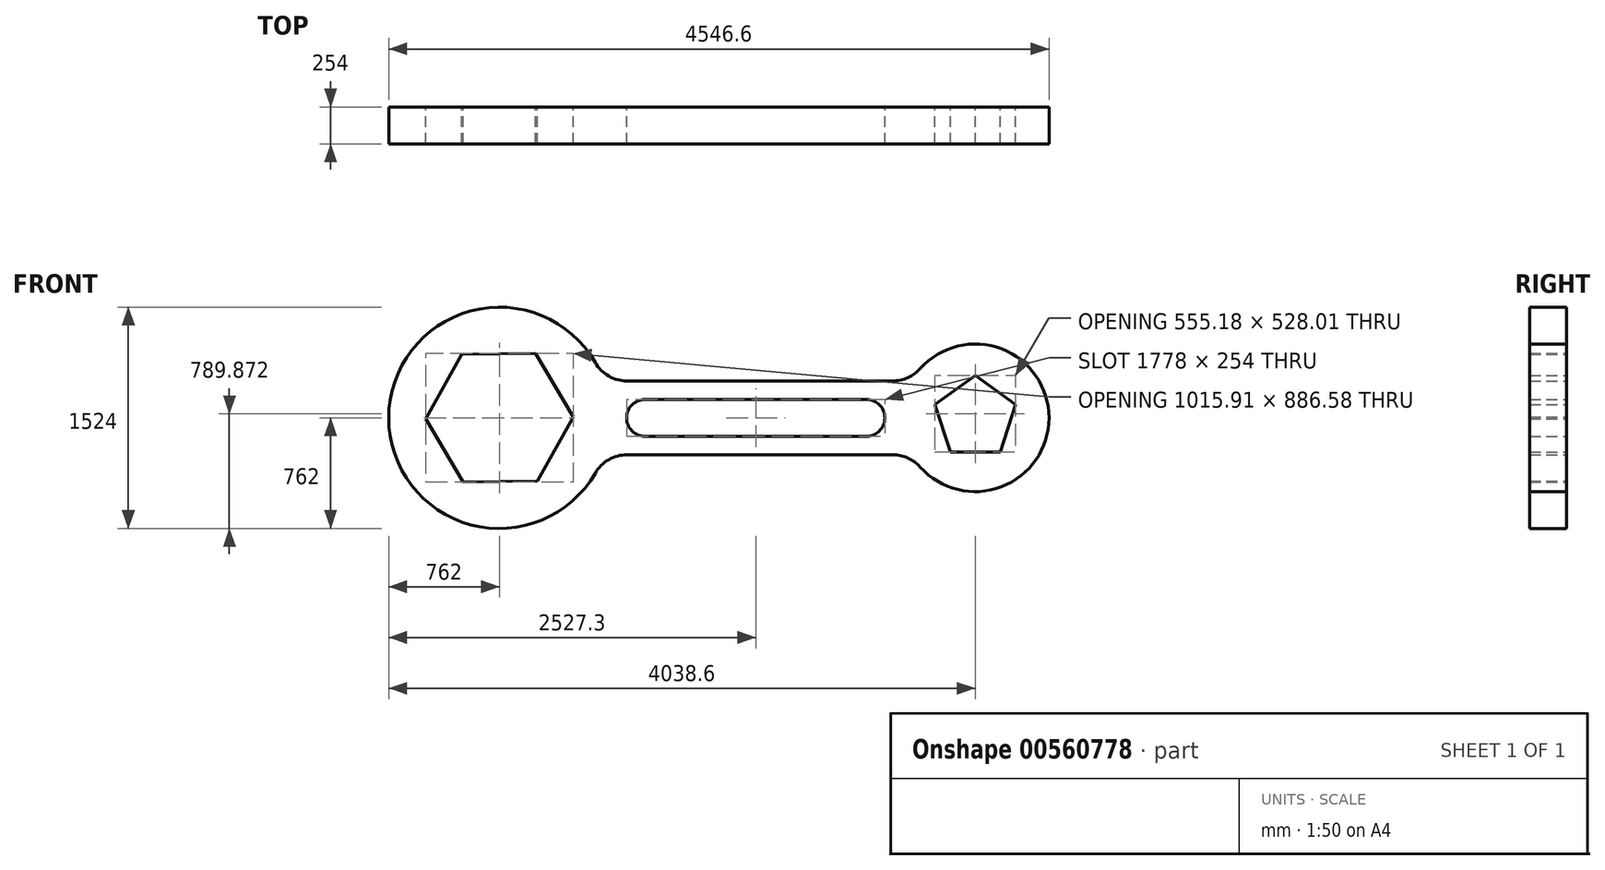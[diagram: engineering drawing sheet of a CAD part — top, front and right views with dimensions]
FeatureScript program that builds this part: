
annotation { "Feature Type Name" : "Feature", "Feature Type Description" : "" }
export const myFeature = defineFeature(function(context is Context, id is Id, definition is map)
    precondition{}
    {
        {
            var Q0;
            Q0=qCreatedBy(makeId("Front.planeOp"),FACE);
            var sketch = newSketch(context, id + "F0", { "sketchPlane" : qUnion([Q0])});
            skCircle(sketch, "E0", {"center": v(0, 0) * mm, "radius": 762 * mm});
            skCircle(sketch, "E1", {"center": v(3276.6, 0) * mm, "radius": 508 * mm});
            skLineSegment(sketch, "E2", {"start": v(1765.3, -254) * mm, "end": v(2708.64, -254) * mm});
            skLineSegment(sketch, "E3", {"start": v(1765.3, -254) * mm, "end": v(879.88, -254) * mm});
            skLineSegment(sketch, "E4", {"start": v(1765.3, 254) * mm, "end": v(879.88, 254) * mm});
            skLineSegment(sketch, "E5", {"start": v(1765.3, 254) * mm, "end": v(2708.64, 254) * mm});
            skArc(sketch, "E6", {"start": v(879.88, -254) * mm, "mid": v(752.88, -288.03) * mm, "end": v(659.91, -381) * mm});
            skArc(sketch, "E7", {"start": v(659.91, 381) * mm, "mid": v(752.88, 288.03) * mm, "end": v(879.88, 254) * mm});
            skArc(sketch, "E8", {"start": v(2708.64, 254) * mm, "mid": v(2812.33, 276.13) * mm, "end": v(2897.96, 338.67) * mm});
            skArc(sketch, "E9", {"start": v(2897.96, -338.67) * mm, "mid": v(2812.33, -276.13) * mm, "end": v(2708.64, -254) * mm});
            skPoint(sketch, "E10.orphan", {"position": v(762, 0) * mm});
            skPoint(sketch, "E11.orphan", {"position": v(2768.6, 0) * mm});
            skPoint(sketch, "E12.orphan", {"position": v(2654.3, 127) * mm});
            skLineSegment(sketch, "E13", {"start": v(1765.3, 127) * mm, "end": v(1003.3, 127) * mm});
            skLineSegment(sketch, "E14", {"start": v(1003.3, -127) * mm, "end": v(2527.3, -127) * mm});
            skLineSegment(sketch, "E15", {"start": v(2527.3, 127) * mm, "end": v(1765.3, 127) * mm});
            skArc(sketch, "E16", {"start": v(1003.3, 127) * mm, "mid": v(876.3, 0) * mm, "end": v(1003.3, -127) * mm});
            skArc(sketch, "E17", {"start": v(2527.3, -127) * mm, "mid": v(2654.3, 0) * mm, "end": v(2527.3, 127) * mm});
            skPoint(sketch, "E18.start.orphan", {"position": v(1765.3, 0) * mm});
            skLineSegment(sketch, "E19.0", {"start": v(248.1, 443.3) * mm, "end": v(507.95, 6.78) * mm});
            skLineSegment(sketch, "E19.1", {"start": v(507.95, 6.78) * mm, "end": v(259.85, -436.51) * mm});
            skLineSegment(sketch, "E19.2", {"start": v(259.85, -436.51) * mm, "end": v(-248.1, -443.3) * mm});
            skLineSegment(sketch, "E19.3", {"start": v(-248.1, -443.3) * mm, "end": v(-507.95, -6.78) * mm});
            skLineSegment(sketch, "E19.4", {"start": v(-507.95, -6.78) * mm, "end": v(-259.85, 436.51) * mm});
            skLineSegment(sketch, "E19.5", {"start": v(-259.85, 436.51) * mm, "end": v(248.1, 443.3) * mm});
            skLineSegment(sketch, "E20.0", {"start": v(3276.6, 291.87) * mm, "end": v(3554.19, 90.2) * mm});
            skLineSegment(sketch, "E20.1", {"start": v(3554.19, 90.2) * mm, "end": v(3448.16, -236.13) * mm});
            skLineSegment(sketch, "E20.2", {"start": v(3448.16, -236.13) * mm, "end": v(3105.04, -236.13) * mm});
            skLineSegment(sketch, "E20.3", {"start": v(3105.04, -236.13) * mm, "end": v(2999.01, 90.2) * mm});
            skLineSegment(sketch, "E20.4", {"start": v(2999.01, 90.2) * mm, "end": v(3276.6, 291.87) * mm});
            skSolve(sketch);
        }
        {
            var Q0;
            Q0=makeQuery(id+"F0.imprint","IMPRINT",FACE,{"disambiguationData":[TD([[makeQuery(id+"F0.imprint","IMPRINT",EDGE,{"derivedFrom":sQuery(id+"F0.wireOp",EDGE,"E20.0")}),1.0]])]});
            var Q1;
            Q1=makeQuery(id+"F0.imprint","IMPRINT",FACE,{"disambiguationData":[TD([[makeQuery(id+"F0.imprint","IMPRINT",EDGE,{"derivedFrom":sQuery(id+"F0.wireOp",EDGE,"E2")}),1.0]])]});
            var Q2;
            Q2=makeQuery(id+"F0.imprint","IMPRINT",FACE,{"disambiguationData":[TD([[makeQuery(id+"F0.imprint","IMPRINT",EDGE,{"derivedFrom":sQuery(id+"F0.wireOp",EDGE,"E19.0")}),1.0]])]});
            extrude(context, id + "F1", {"entities" : qUnion([Q0, Q1, Q2]), "depth" : 254 * mm, "offsetDistance" : 25.4 * mm});
        }
    });
